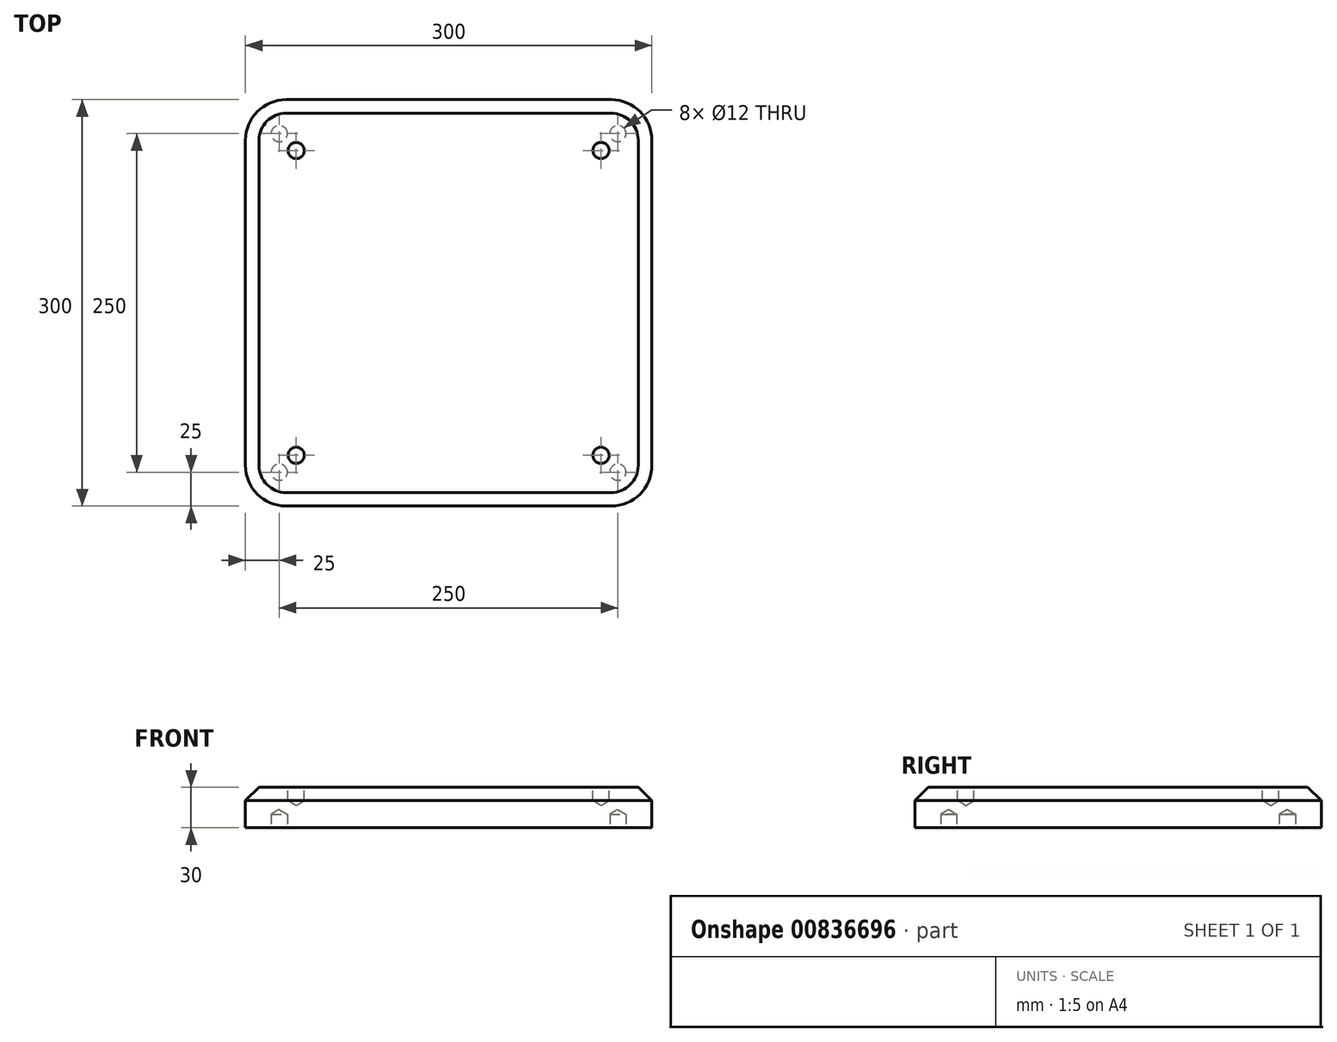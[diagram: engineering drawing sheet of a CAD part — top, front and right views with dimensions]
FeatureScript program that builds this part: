
annotation { "Feature Type Name" : "Feature", "Feature Type Description" : "" }
export const myFeature = defineFeature(function(context is Context, id is Id, definition is map)
    precondition{}
    {
        {
            var Q0;
            Q0=qCreatedBy(makeId("Top.planeOp"),FACE);
            var sketch = newSketch(context, id + "F0", { "sketchPlane" : qUnion([Q0])});
            skLineSegment(sketch, "E0.bottom", {"start": v(-150, -150) * mm, "end": v(150, -150) * mm});
            skLineSegment(sketch, "E0.top", {"start": v(-150, 150) * mm, "end": v(150, 150) * mm});
            skLineSegment(sketch, "E0.left", {"start": v(-150, -150) * mm, "end": v(-150, 150) * mm});
            skLineSegment(sketch, "E0.right", {"start": v(150, -150) * mm, "end": v(150, 150) * mm});
            skSolve(sketch);
        }
        {
            var Q0;
            Q0 = qSketchRegion(id + "F0", true);
            extrude(context, id + "F1", {"entities" : qUnion([Q0]), "depth" : 30 * mm, "offsetDistance" : 25 * mm});
        }
        {
            var Q0;
            Q0=makeQuery(id+"F1.opExtrude","CAP_FACE",FACE,{"disambiguationData":[OSD([sQuery(id+"F0.wireOp",EDGE,"E0.bottom"),sQuery(id+"F0.wireOp",EDGE,"E0.top"),sQuery(id+"F0.wireOp",EDGE,"E0.left"),sQuery(id+"F0.wireOp",EDGE,"E0.right")])],"isStart":false});
            var sketch = newSketch(context, id + "F2", { "sketchPlane" : qUnion([Q0])});
            skCircle(sketch, "E1", {"center": v(-112.5, 112.5) * mm, "radius": 6 * mm});
            skCircle(sketch, "E2.0.1.0", {"center": v(-112.5, -112.5) * mm, "radius": 6 * mm});
            skCircle(sketch, "E2.1.0.0", {"center": v(112.5, 112.5) * mm, "radius": 6 * mm});
            skCircle(sketch, "E2.1.1.0", {"center": v(112.5, -112.5) * mm, "radius": 6 * mm});
            skLineSegment(sketch, "E2.direction1", {"start": v(-112.5, 112.5) * mm, "end": v(112.5, 112.5) * mm, "construction": true});
            skLineSegment(sketch, "E2.direction2", {"start": v(-112.5, 112.5) * mm, "end": v(-112.5, -112.5) * mm, "construction": true});
            skSolve(sketch);
        }
        {
            var Q0;
            Q0=makeQuery(id+"F1.opExtrude","SWEPT_EDGE",EDGE,{"disambiguationData":[OSD([sQuery(id+"F0.wireOp",EDGE,"E0.top"),sQuery(id+"F0.wireOp",EDGE,"E0.left")])]});
            var Q1;
            Q1=makeQuery(id+"F1.opExtrude","SWEPT_EDGE",EDGE,{"disambiguationData":[OSD([sQuery(id+"F0.wireOp",EDGE,"E0.top"),sQuery(id+"F0.wireOp",EDGE,"E0.right")])]});
            var Q2;
            Q2=makeQuery(id+"F1.opExtrude","SWEPT_EDGE",EDGE,{"disambiguationData":[OSD([sQuery(id+"F0.wireOp",EDGE,"E0.bottom"),sQuery(id+"F0.wireOp",EDGE,"E0.left")])]});
            var Q3;
            Q3=makeQuery(id+"F1.opExtrude","SWEPT_EDGE",EDGE,{"disambiguationData":[OSD([sQuery(id+"F0.wireOp",EDGE,"E0.bottom"),sQuery(id+"F0.wireOp",EDGE,"E0.right")])]});
            fillet(context, id + "F3", {"entities" : qUnion([Q0, Q1, Q2, Q3]), "radius" : 30 * mm, "tangentPropagation" : true, "allowEdgeOverflow" : false});
        }
        {
            var Q0;
            Q0=makeQuery(id+"F1.opExtrude","CAP_EDGE",EDGE,{"disambiguationData":[OSD([sQuery(id+"F0.wireOp",EDGE,"E0.top")])],"isStart":false});
            chamfer(context, id + "F4", {"entities" : qUnion([Q0]), "width" : 10 * mm, "tangentPropagation" : true});
        }
        {
            var Q0;
            Q0=sQuery(id+"F2.wireOp",VERTEX,"E2.1.1.0.center");
            var Q1;
            Q1=sQuery(id+"F2.wireOp",VERTEX,"E2.direction1.end");
            var Q2;
            Q2=sQuery(id+"F2.wireOp",VERTEX,"E2.direction1.start");
            var Q3;
            Q3=sQuery(id+"F2.wireOp",VERTEX,"E2.direction2.end");
            var Q4;
            Q4=makeQuery(id+"F1.opExtrude","SWEPT_BODY",BODY,{"disambiguationData":[OSD([sQuery(id+"F0.wireOp",EDGE,"E0.bottom"),sQuery(id+"F0.wireOp",EDGE,"E0.top"),sQuery(id+"F0.wireOp",EDGE,"E0.left"),sQuery(id+"F0.wireOp",EDGE,"E0.right")])]});
            hole(context, id + "F5", {"style" : HoleStyle.SIMPLE, "endStyle" : HoleEndStyle.BLIND, "holeDiameter" : 12 * mm, "majorDiameter" : 5 * mm, "holeDepth" : 10 * mm, "isTappedThrough" : true, "tappedDepth" : 12 * mm, "tapClearance" : 3, "locations" : qUnion([Q0, Q1, Q2, Q3]), "scope" : qUnion([Q4])});
        }
        {
            var Q0;
            Q0=makeQuery(id+"F0.imprint","IMPRINT",FACE,{"disambiguationData":[TD([[makeQuery(id+"F0.imprint","IMPRINT",EDGE,{"derivedFrom":sQuery(id+"F0.wireOp",EDGE,"E0.bottom")}),1.0]])]});
            var sketch = newSketch(context, id + "F6", { "sketchPlane" : qUnion([Q0])});
            skCircle(sketch, "E3", {"center": v(-125, -125) * mm, "radius": 6 * mm});
            skCircle(sketch, "E4.0.1.0", {"center": v(-125, 125) * mm, "radius": 6 * mm});
            skCircle(sketch, "E4.1.0.0", {"center": v(125, -125) * mm, "radius": 6 * mm});
            skCircle(sketch, "E4.1.1.0", {"center": v(125, 125) * mm, "radius": 6 * mm});
            skLineSegment(sketch, "E4.direction1", {"start": v(-125, -125) * mm, "end": v(125, -125) * mm, "construction": true});
            skLineSegment(sketch, "E4.direction2", {"start": v(-125, -125) * mm, "end": v(-125, 125) * mm, "construction": true});
            skSolve(sketch);
        }
        {
            var Q0;
            Q0=sQuery(id+"F6.wireOp",VERTEX,"E4.direction1.start");
            var Q1;
            Q1=sQuery(id+"F6.wireOp",VERTEX,"E4.direction2.end");
            var Q2;
            Q2=sQuery(id+"F6.wireOp",VERTEX,"E4.1.1.0.center");
            var Q3;
            Q3=sQuery(id+"F6.wireOp",VERTEX,"E4.direction1.end");
            var Q4;
            Q4=makeQuery(id+"F1.opExtrude","SWEPT_BODY",BODY,{"disambiguationData":[OSD([sQuery(id+"F0.wireOp",EDGE,"E0.bottom"),sQuery(id+"F0.wireOp",EDGE,"E0.top"),sQuery(id+"F0.wireOp",EDGE,"E0.left"),sQuery(id+"F0.wireOp",EDGE,"E0.right")])]});
            hole(context, id + "F7", {"style" : HoleStyle.SIMPLE, "endStyle" : HoleEndStyle.BLIND, "oppositeDirection" : true, "holeDiameter" : 12 * mm, "majorDiameter" : 5 * mm, "holeDepth" : 10 * mm, "isTappedThrough" : true, "tappedDepth" : 12 * mm, "tapClearance" : 3, "locations" : qUnion([Q0, Q1, Q2, Q3]), "scope" : qUnion([Q4])});
        }
    });
